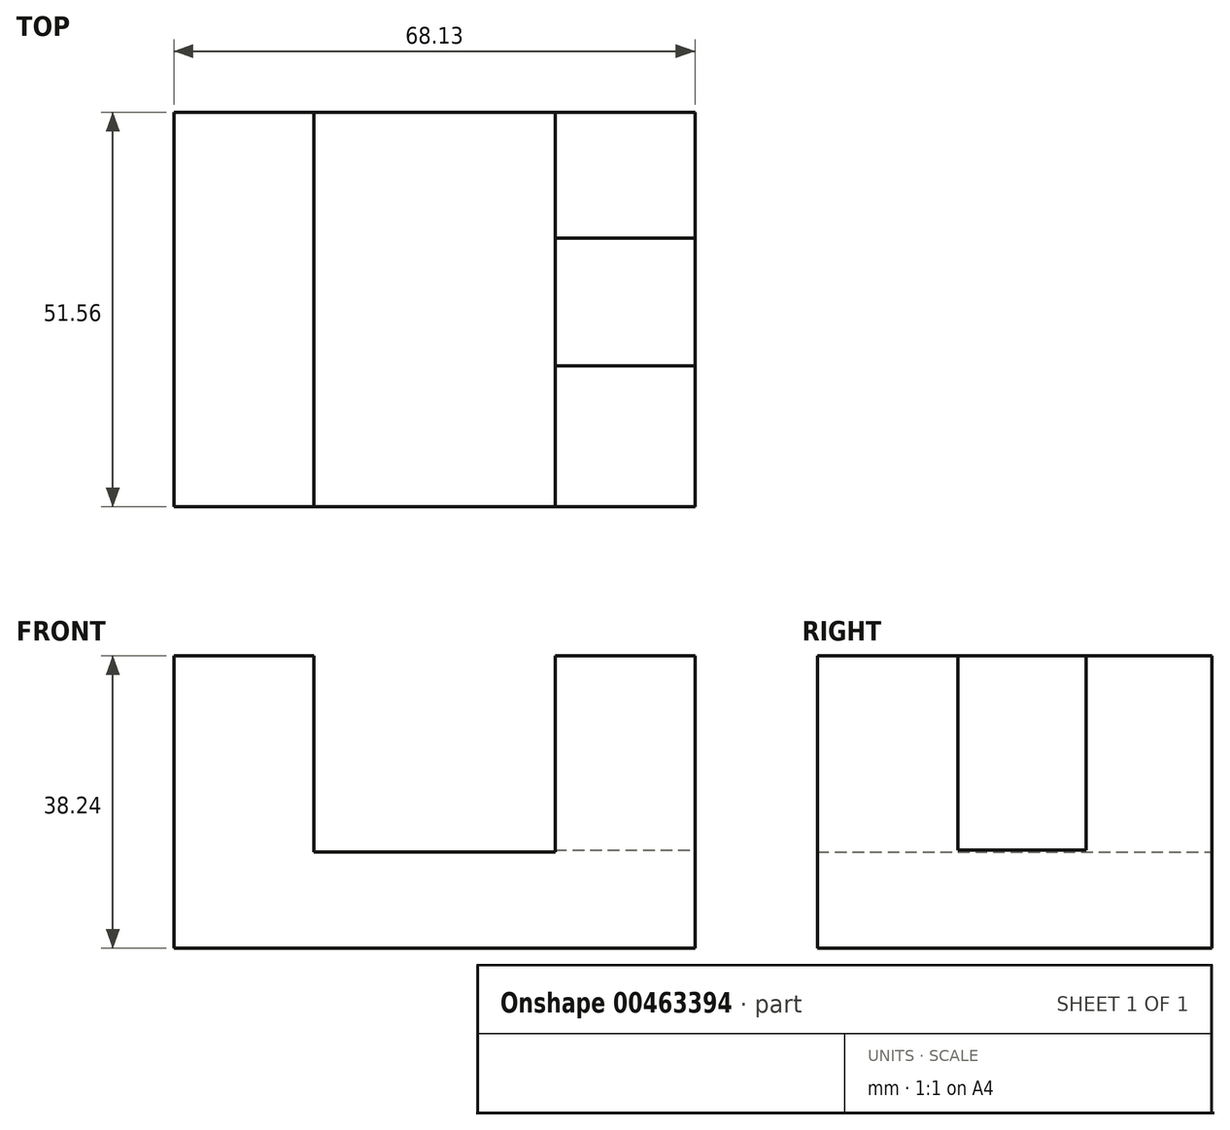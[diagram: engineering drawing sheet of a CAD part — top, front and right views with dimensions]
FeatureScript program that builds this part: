
annotation { "Feature Type Name" : "Feature", "Feature Type Description" : "" }
export const myFeature = defineFeature(function(context is Context, id is Id, definition is map)
    precondition{}
    {
        {
            var Q0;
            Q0=qCreatedBy(makeId("Front.planeOp"),FACE);
            var sketch = newSketch(context, id + "F0", { "sketchPlane" : qUnion([Q0])});
            skLineSegment(sketch, "E0.bottom", {"start": v(0, 0) * mm, "end": v(68.13, 0) * mm});
            skLineSegment(sketch, "E0.top", {"start": v(0, 38.24) * mm, "end": v(18.28, 38.24) * mm});
            skLineSegment(sketch, "E0.left", {"start": v(0, 0) * mm, "end": v(0, 38.24) * mm});
            skLineSegment(sketch, "E0.right", {"start": v(68.13, 0) * mm, "end": v(68.13, 38.24) * mm});
            skLineSegment(sketch, "E1.top", {"start": v(49.85, 12.56) * mm, "end": v(18.28, 12.56) * mm});
            skLineSegment(sketch, "E1.left", {"start": v(49.85, 38.24) * mm, "end": v(49.85, 12.56) * mm});
            skLineSegment(sketch, "E1.right", {"start": v(18.28, 38.24) * mm, "end": v(18.28, 12.56) * mm});
            skPoint(sketch, "E1.middle", {"position": v(34.06, 25.4) * mm});
            skLineSegment(sketch, "E2.trimOffspring", {"start": v(49.85, 38.24) * mm, "end": v(68.13, 38.24) * mm});
            skSolve(sketch);
        }
        {
            var Q0;
            Q0=makeQuery(id+"F0.imprint","IMPRINT",FACE,{"disambiguationData":[TD([[makeQuery(id+"F0.imprint","IMPRINT",EDGE,{"derivedFrom":sQuery(id+"F0.wireOp",EDGE,"E0.bottom")}),1.0]])]});
            extrude(context, id + "F1", {"entities" : qUnion([Q0]), "depth" : 51.56 * mm});
        }
        {
            var Q0;
            Q0=makeQuery(id+"F1.opExtrude","SWEPT_FACE",FACE,{"disambiguationData":[OSD([sQuery(id+"F0.wireOp",EDGE,"E2.trimOffspring")])]});
            var sketch = newSketch(context, id + "F2", { "sketchPlane" : qUnion([Q0])});
            skLineSegment(sketch, "E3.bottom", {"start": v(49.85, -33.16) * mm, "end": v(68.13, -33.16) * mm});
            skLineSegment(sketch, "E3.top", {"start": v(49.85, -16.44) * mm, "end": v(68.13, -16.44) * mm});
            skLineSegment(sketch, "E3.left", {"start": v(49.85, -33.16) * mm, "end": v(49.85, -16.44) * mm});
            skLineSegment(sketch, "E3.right", {"start": v(68.13, -33.16) * mm, "end": v(68.13, -16.44) * mm});
            skSolve(sketch);
        }
        {
            var Q0;
            Q0 = qSketchRegion(id + "F2", true);
            extrude(context, id + "F3", {"entities" : qUnion([Q0]), "operationType" : NewBodyOperationType.REMOVE, "oppositeDirection" : true, "depth" : 25.4 * mm});
        }
    });
